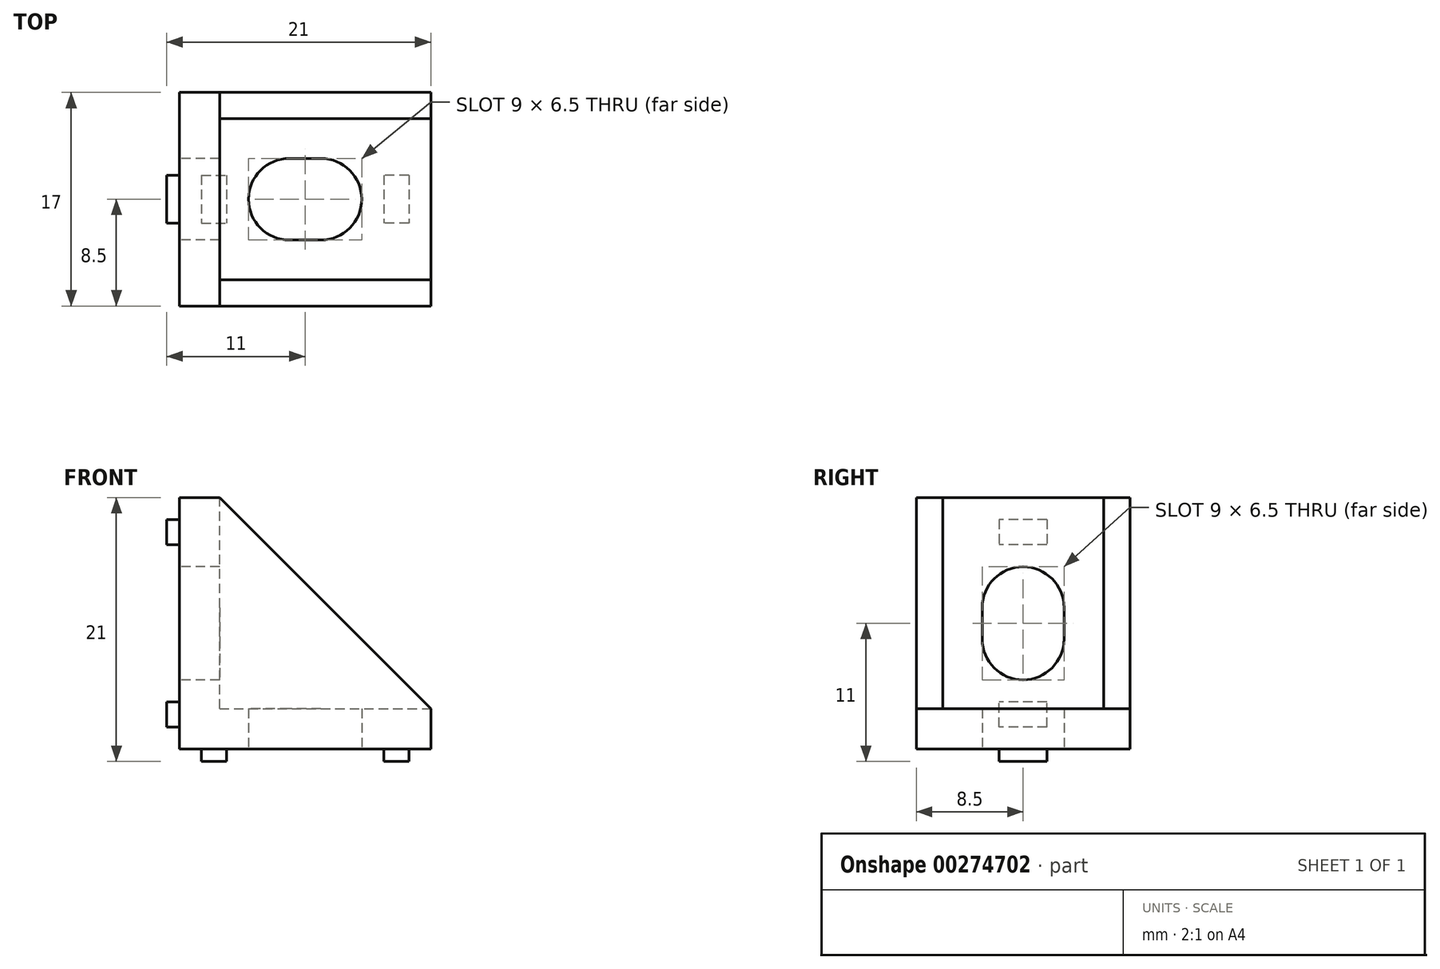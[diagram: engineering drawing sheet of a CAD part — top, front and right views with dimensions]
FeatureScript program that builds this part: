
annotation { "Feature Type Name" : "Feature", "Feature Type Description" : "" }
export const myFeature = defineFeature(function(context is Context, id is Id, definition is map)
    precondition{}
    {
        {
            var Q0;
            Q0=qCreatedBy(makeId("Front.planeOp"),FACE);
            var sketch = newSketch(context, id + "F0", { "sketchPlane" : qUnion([Q0])});
            skLineSegment(sketch, "E0", {"start": v(0, 0) * mm, "end": v(20, 0) * mm});
            skLineSegment(sketch, "E1", {"start": v(20, 0) * mm, "end": v(20, 3.2) * mm});
            skLineSegment(sketch, "E2", {"start": v(0, 0) * mm, "end": v(0, 20) * mm});
            skLineSegment(sketch, "E3", {"start": v(0, 20) * mm, "end": v(3.2, 20) * mm});
            skLineSegment(sketch, "E4", {"start": v(3.2, 20) * mm, "end": v(20, 3.2) * mm});
            skSolve(sketch);
        }
        {
            var Q0;
            Q0 = qSketchRegion(id + "F0", true);
            extrude(context, id + "F1", {"entities" : qUnion([Q0]), "depth" : 17 * mm});
        }
        {
            var Q0;
            Q0=makeQuery(id+"F1.opExtrude","SWEPT_FACE",FACE,{"disambiguationData":[OSD([sQuery(id+"F0.wireOp",EDGE,"E1")])]});
            var sketch = newSketch(context, id + "F2", { "sketchPlane" : qUnion([Q0])});
            skLineSegment(sketch, "E5.bottom", {"start": v(-2.1, 3.2) * mm, "end": v(-14.9, 3.2) * mm});
            skLineSegment(sketch, "E5.top", {"start": v(-2.1, 20) * mm, "end": v(-14.9, 20) * mm});
            skLineSegment(sketch, "E5.left", {"start": v(-2.1, 3.2) * mm, "end": v(-2.1, 20) * mm});
            skLineSegment(sketch, "E5.right", {"start": v(-14.9, 3.2) * mm, "end": v(-14.9, 20) * mm});
            skSolve(sketch);
        }
        {
            var Q0;
            Q0 = qSketchRegion(id + "F2", true);
            extrude(context, id + "F3", {"entities" : qUnion([Q0]), "operationType" : NewBodyOperationType.REMOVE, "oppositeDirection" : true, "depth" : 16.8 * mm});
        }
        {
            var Q0;
            Q0=makeQuery(id+"F1.opExtrude","SWEPT_FACE",FACE,{"disambiguationData":[OSD([sQuery(id+"F0.wireOp",EDGE,"E2")])]});
            var sketch = newSketch(context, id + "F4", { "sketchPlane" : qUnion([Q0])});
            skLineSegment(sketch, "E6", {"start": v(8.5, 8.75) * mm, "end": v(8.5, 11.25) * mm, "construction": true});
            skPoint(sketch, "E6.startSnap0", {"position": v(8.5, 0) * mm});
            skPoint(sketch, "E7", {"position": v(8.5, 10) * mm});
            skPoint(sketch, "E8", {"position": v(17, 10) * mm});
            skArc(sketch, "E9.0.startCap", {"start": v(11.75, 8.75) * mm, "mid": v(8.5, 5.5) * mm, "end": v(5.25, 8.75) * mm});
            skArc(sketch, "E9.0.endCap", {"start": v(5.25, 11.25) * mm, "mid": v(8.5, 14.5) * mm, "end": v(11.75, 11.25) * mm});
            skLineSegment(sketch, "E9.0.left", {"start": v(5.25, 8.75) * mm, "end": v(5.25, 11.25) * mm});
            skLineSegment(sketch, "E9.0.right", {"start": v(11.75, 8.75) * mm, "end": v(11.75, 11.25) * mm});
            skSolve(sketch);
        }
        {
            var Q0;
            Q0 = qSketchRegion(id + "F4", true);
            extrude(context, id + "F5", {"entities" : qUnion([Q0]), "oppositeDirection" : true, "depth" : 5 * mm});
        }
        {
            var Q0;
            Q0=makeQuery(id+"F3.boolean.opBoolean","INTERSECT",EDGE,{"derivedFrom":[makeQuery(id+"F1.opExtrude","SWEPT_FACE",FACE,{"disambiguationData":[OSD([sQuery(id+"F0.wireOp",EDGE,"E4")])]}),makeQuery(id+"F3.opExtrude","SWEPT_FACE",FACE,{"disambiguationData":[OSD([sQuery(id+"F2.wireOp",EDGE,"E5.left")])]})]});
            cPoint(context, id + "F6", {"entities" : qUnion([Q0]), "parameter" : 0.5});
        }
        {
            var Q0;
            Q0=makeQuery(id+"F3.boolean.opBoolean","INTERSECT",EDGE,{"derivedFrom":[makeQuery(id+"F1.opExtrude","SWEPT_FACE",FACE,{"disambiguationData":[OSD([sQuery(id+"F0.wireOp",EDGE,"E4")])]}),makeQuery(id+"F3.opExtrude","SWEPT_FACE",FACE,{"disambiguationData":[OSD([sQuery(id+"F2.wireOp",EDGE,"E5.right")])]})]});
            cPoint(context, id + "F7", {"entities" : qUnion([Q0]), "parameter" : 0.5});
        }
        {
            var Q0;
            Q0 = qCreatedBy(id + "F6" ,VERTEX);
            var Q1;
            Q1=makeQuery(id+"F3.boolean.opBoolean","COPY",VERTEX,{"derivedFrom":makeQuery(id+"F3.opExtrude","CAP_VERTEX",VERTEX,{"disambiguationData":[OSD([sQuery(id+"F0.wireOp",EDGE,"E1"),sQuery(id+"F0.wireOp",EDGE,"E4"),sQuery(id+"F2.wireOp",EDGE,"E5.bottom"),sQuery(id+"F2.wireOp",EDGE,"E5.left")])],"isStart":false})});
            var Q2;
            Q2 = qCreatedBy(id + "F7" ,VERTEX);
            cPlane(context, id + "F8", {"entities" : qUnion([Q0, Q1, Q2]), "cplaneType" : CPlaneType.THREE_POINT, "offset" : 25 * mm, "width" : 150 * mm, "height" : 150 * mm});
        }
        {
            var Q0;
            Q0=makeQuery(id+"F5.opExtrude","SWEPT_BODY",BODY,{"disambiguationData":[OSD([sQuery(id+"F4.wireOp",EDGE,"E9.0.startCap"),sQuery(id+"F4.wireOp",EDGE,"E9.0.endCap"),sQuery(id+"F4.wireOp",EDGE,"E9.0.left"),sQuery(id+"F4.wireOp",EDGE,"E9.0.right")])]});
            var Q1;
            Q1=qCreatedBy(id+"F8.planeOp",FACE);
            mirror(context, id + "F9", {"entities" : qUnion([Q0]), "mirrorPlane" : qUnion([Q1])});
        }
        {
            var Q0;
            Q0=makeQuery(id+"F5.opExtrude","SWEPT_BODY",BODY,{"disambiguationData":[OSD([sQuery(id+"F4.wireOp",EDGE,"E9.0.startCap"),sQuery(id+"F4.wireOp",EDGE,"E9.0.endCap"),sQuery(id+"F4.wireOp",EDGE,"E9.0.left"),sQuery(id+"F4.wireOp",EDGE,"E9.0.right")])]});
            var Q1;
            Q1=makeQuery(id+"F9.opPattern","COPY",BODY,{"derivedFrom":makeQuery(id+"F5.opExtrude","SWEPT_BODY",BODY,{"disambiguationData":[OSD([sQuery(id+"F4.wireOp",EDGE,"E9.0.startCap"),sQuery(id+"F4.wireOp",EDGE,"E9.0.endCap"),sQuery(id+"F4.wireOp",EDGE,"E9.0.left"),sQuery(id+"F4.wireOp",EDGE,"E9.0.right")])]}),"instanceName":"1"});
            var Q2;
            Q2=makeQuery(id+"F1.opExtrude","SWEPT_BODY",BODY,{"disambiguationData":[OSD([sQuery(id+"F0.wireOp",EDGE,"E0"),sQuery(id+"F0.wireOp",EDGE,"E1"),sQuery(id+"F0.wireOp",EDGE,"E2"),sQuery(id+"F0.wireOp",EDGE,"E3"),sQuery(id+"F0.wireOp",EDGE,"E4")])]});
            booleanBodies(context, id + "F10", {"operationType" : BooleanOperationType.SUBTRACTION, "tools" : qUnion([Q0, Q1]), "targets" : qUnion([Q2])});
        }
        {
            var Q0;
            Q0=makeQuery(id+"F1.opExtrude","SWEPT_FACE",FACE,{"disambiguationData":[OSD([sQuery(id+"F0.wireOp",EDGE,"E2")])]});
            var sketch = newSketch(context, id + "F11", { "sketchPlane" : qUnion([Q0])});
            skLineSegment(sketch, "E10.bottom", {"start": v(6.6, 18.25) * mm, "end": v(10.4, 18.25) * mm});
            skLineSegment(sketch, "E10.top", {"start": v(6.6, 16.25) * mm, "end": v(10.4, 16.25) * mm});
            skLineSegment(sketch, "E10.left", {"start": v(6.6, 18.25) * mm, "end": v(6.6, 16.25) * mm});
            skLineSegment(sketch, "E10.right", {"start": v(10.4, 18.25) * mm, "end": v(10.4, 16.25) * mm});
            skPoint(sketch, "E11", {"position": v(8.5, 16.25) * mm});
            skPoint(sketch, "E12", {"position": v(8.5, 14.5) * mm});
            skPoint(sketch, "E13", {"position": v(5.25, 10) * mm});
            skLineSegment(sketch, "E14", {"start": v(5.25, 10) * mm, "end": v(11.75, 10) * mm, "construction": true});
            skLineSegment(sketch, "E15.MirrorCS", {"start": v(6.6, 3.75) * mm, "end": v(10.4, 3.75) * mm});
            skLineSegment(sketch, "E16.MirrorCS", {"start": v(6.6, 1.75) * mm, "end": v(6.6, 3.75) * mm});
            skLineSegment(sketch, "E17.MirrorCS", {"start": v(10.4, 1.75) * mm, "end": v(10.4, 3.75) * mm});
            skLineSegment(sketch, "E18.MirrorCS", {"start": v(6.6, 1.75) * mm, "end": v(10.4, 1.75) * mm});
            skSolve(sketch);
        }
        {
            var Q0;
            Q0 = qSketchRegion(id + "F11", true);
            extrude(context, id + "F12", {"entities" : qUnion([Q0]), "depth" : 1 * mm});
        }
        {
            var Q0;
            Q0=makeQuery(id+"F12.opExtrude","SWEPT_BODY",BODY,{"disambiguationData":[OSD([sQuery(id+"F11.wireOp",EDGE,"E10.bottom"),sQuery(id+"F11.wireOp",EDGE,"E10.top"),sQuery(id+"F11.wireOp",EDGE,"E10.left"),sQuery(id+"F11.wireOp",EDGE,"E10.right")])]});
            var Q1;
            Q1=makeQuery(id+"F12.opExtrude","SWEPT_BODY",BODY,{"disambiguationData":[OSD([sQuery(id+"F11.wireOp",EDGE,"E15.MirrorCS"),sQuery(id+"F11.wireOp",EDGE,"E16.MirrorCS"),sQuery(id+"F11.wireOp",EDGE,"E17.MirrorCS"),sQuery(id+"F11.wireOp",EDGE,"E18.MirrorCS")])]});
            var Q2;
            Q2=qCreatedBy(id+"F8.planeOp",FACE);
            mirror(context, id + "F13", {"operationType" : NewBodyOperationType.ADD, "entities" : qUnion([Q0, Q1]), "mirrorPlane" : qUnion([Q2])});
        }
    });
